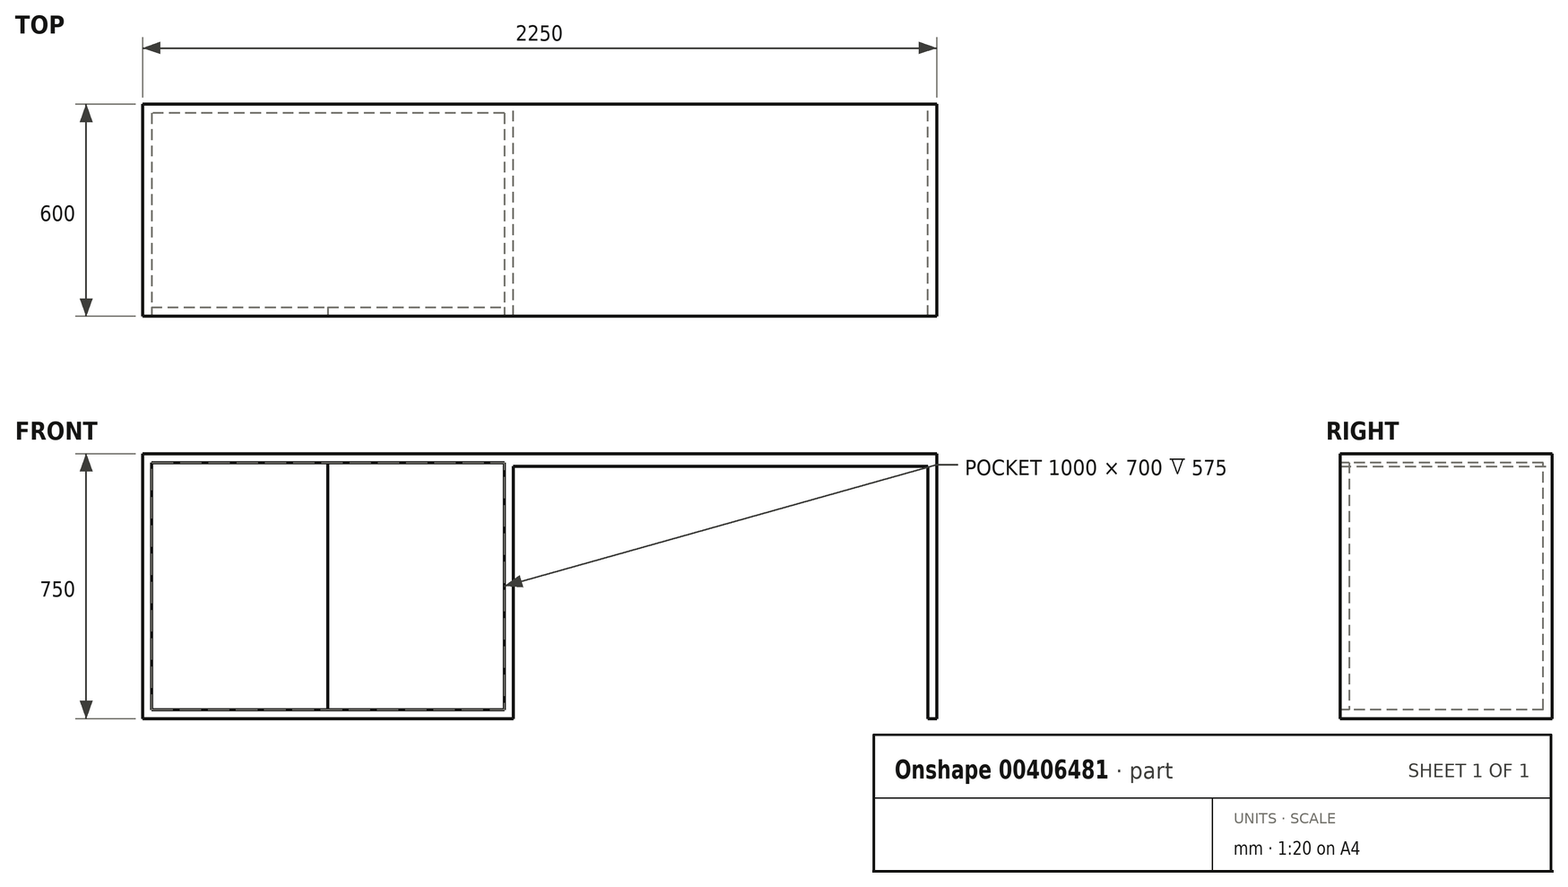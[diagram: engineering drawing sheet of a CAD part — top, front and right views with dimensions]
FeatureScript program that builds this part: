
annotation { "Feature Type Name" : "Feature", "Feature Type Description" : "" }
export const myFeature = defineFeature(function(context is Context, id is Id, definition is map)
    precondition{}
    {
        {
            var Q0;
            Q0=qCreatedBy(makeId("Front.planeOp"),FACE);
            var sketch = newSketch(context, id + "F0", { "sketchPlane" : qUnion([Q0])});
            skLineSegment(sketch, "E0.bottom", {"start": v(-1125, 0) * mm, "end": v(-75, 0) * mm});
            skLineSegment(sketch, "E0.top", {"start": v(-1125, 750) * mm, "end": v(-75, 750) * mm});
            skLineSegment(sketch, "E0.left", {"start": v(-1125, 0) * mm, "end": v(-1125, 750) * mm});
            skLineSegment(sketch, "E0.right", {"start": v(-75, 0) * mm, "end": v(-75, 750) * mm});
            skLineSegment(sketch, "E1.bottom", {"start": v(-75, 750) * mm, "end": v(1125, 750) * mm});
            skLineSegment(sketch, "E1.top", {"start": v(-75, 715) * mm, "end": v(1125, 715) * mm});
            skLineSegment(sketch, "E1.left", {"start": v(-75, 750) * mm, "end": v(-75, 715) * mm});
            skLineSegment(sketch, "E1.right", {"start": v(1125, 750) * mm, "end": v(1125, 715) * mm});
            skLineSegment(sketch, "E2.bottom", {"start": v(1125, 715) * mm, "end": v(1100, 715) * mm});
            skLineSegment(sketch, "E2.top", {"start": v(1125, 0) * mm, "end": v(1100, 0) * mm});
            skLineSegment(sketch, "E2.left", {"start": v(1125, 715) * mm, "end": v(1125, 0) * mm});
            skLineSegment(sketch, "E2.right", {"start": v(1100, 715) * mm, "end": v(1100, 0) * mm});
            skSolve(sketch);
        }
        {
            var Q0;
            Q0 = qSketchRegion(id + "F0", true);
            extrude(context, id + "F1", {"entities" : qUnion([Q0]), "depth" : 600 * mm, "offsetDistance" : 25 * mm});
        }
        {
            var Q0;
            Q0=makeQuery(id+"F1.opExtrude","CAP_FACE",FACE,{"disambiguationData":[OSD([sQuery(id+"F0.wireOp",EDGE,"E0.bottom"),sQuery(id+"F0.wireOp",EDGE,"E0.top"),sQuery(id+"F0.wireOp",EDGE,"E0.left"),sQuery(id+"F0.wireOp",EDGE,"E0.right"),sQuery(id+"F0.wireOp",EDGE,"E1.bottom"),sQuery(id+"F0.wireOp",EDGE,"E1.top"),sQuery(id+"F0.wireOp",EDGE,"E1.right"),sQuery(id+"F0.wireOp",EDGE,"E2.top"),sQuery(id+"F0.wireOp",EDGE,"E2.left"),sQuery(id+"F0.wireOp",EDGE,"E2.right")])],"isStart":false});
            var sketch = newSketch(context, id + "F2", { "sketchPlane" : qUnion([Q0])});
            skLineSegment(sketch, "E3.bottom", {"start": v(-1100, 725) * mm, "end": v(-600, 725) * mm});
            skLineSegment(sketch, "E3.top", {"start": v(-1100, 25) * mm, "end": v(-600, 25) * mm});
            skLineSegment(sketch, "E3.left", {"start": v(-1100, 725) * mm, "end": v(-1100, 25) * mm});
            skLineSegment(sketch, "E3.right", {"start": v(-600, 725) * mm, "end": v(-600, 25) * mm});
            skLineSegment(sketch, "E4.bottom", {"start": v(-600, 725) * mm, "end": v(-100, 725) * mm});
            skLineSegment(sketch, "E4.top", {"start": v(-600, 25) * mm, "end": v(-100, 25) * mm});
            skLineSegment(sketch, "E4.right", {"start": v(-100, 725) * mm, "end": v(-100, 25) * mm});
            skSolve(sketch);
        }
        {
            var Q0;
            Q0=makeQuery(id+"F2.imprint","IMPRINT",FACE,{"disambiguationData":[TD([[makeQuery(id+"F2.imprint","IMPRINT",EDGE,{"derivedFrom":sQuery(id+"F2.wireOp",EDGE,"E3.bottom")}),-1.0]])]});
            var Q1;
            Q1=makeQuery(id+"F2.imprint","IMPRINT",FACE,{"disambiguationData":[TD([[makeQuery(id+"F2.imprint","IMPRINT",EDGE,{"derivedFrom":sQuery(id+"F2.wireOp",EDGE,"E4.bottom")}),-1.0]])]});
            extrude(context, id + "F3", {"entities" : qUnion([Q0, Q1]), "operationType" : NewBodyOperationType.REMOVE, "endBound" : BoundingType.UP_TO_NEXT, "oppositeDirection" : true, "depth" : 25 * mm, "hasOffset" : true, "offsetDistance" : 25 * mm});
        }
        {
            var Q0;
            Q0=makeQuery(id+"F2.imprint","IMPRINT",FACE,{"disambiguationData":[TD([[makeQuery(id+"F2.imprint","IMPRINT",EDGE,{"derivedFrom":sQuery(id+"F2.wireOp",EDGE,"E3.bottom")}),-1.0]])]});
            extrude(context, id + "F4", {"entities" : qUnion([Q0]), "oppositeDirection" : true, "depth" : 25 * mm, "offsetDistance" : 25 * mm});
        }
        {
            var Q0;
            Q0=makeQuery(id+"F2.imprint","IMPRINT",FACE,{"disambiguationData":[TD([[makeQuery(id+"F2.imprint","IMPRINT",EDGE,{"derivedFrom":sQuery(id+"F2.wireOp",EDGE,"E4.bottom")}),-1.0]])]});
            extrude(context, id + "F5", {"entities" : qUnion([Q0]), "oppositeDirection" : true, "depth" : 25 * mm, "offsetDistance" : 25 * mm});
        }
    });
